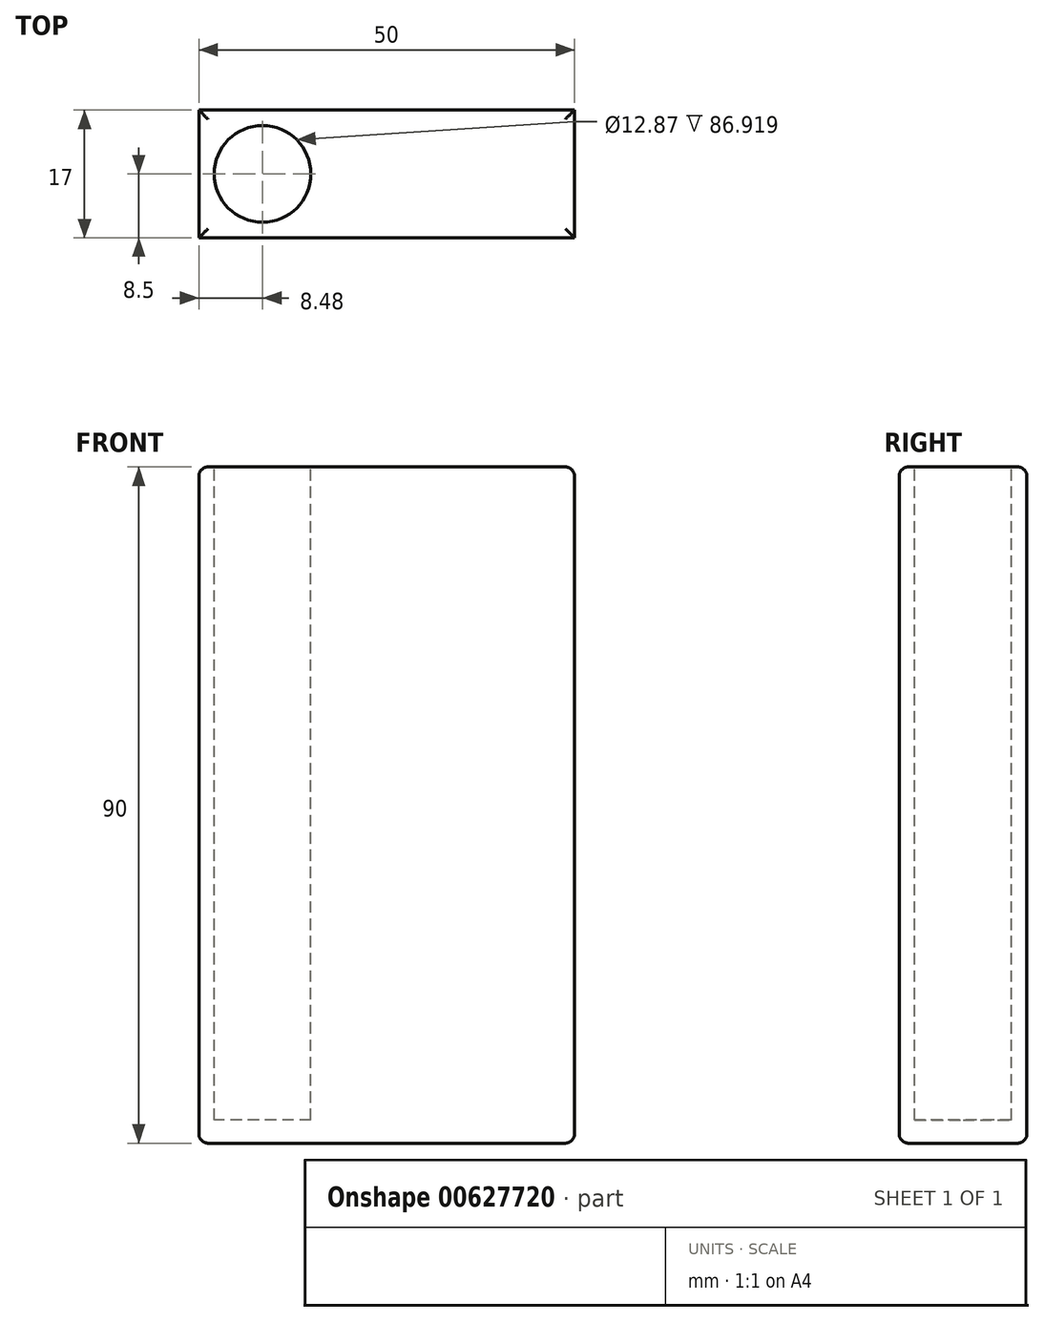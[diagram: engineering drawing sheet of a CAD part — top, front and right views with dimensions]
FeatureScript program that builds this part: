
annotation { "Feature Type Name" : "Feature", "Feature Type Description" : "" }
export const myFeature = defineFeature(function(context is Context, id is Id, definition is map)
    precondition{}
    {
        {
            var Q0;
            Q0=qCreatedBy(makeId("Front.planeOp"),FACE);
            var sketch = newSketch(context, id + "F0", { "sketchPlane" : qUnion([Q0])});
            skLineSegment(sketch, "E0.bottom", {"start": v(0, 90) * mm, "end": v(-50, 90) * mm});
            skLineSegment(sketch, "E0.top", {"start": v(0, 0) * mm, "end": v(-50, 0) * mm});
            skLineSegment(sketch, "E0.left", {"start": v(0, 90) * mm, "end": v(0, 0) * mm});
            skLineSegment(sketch, "E0.right", {"start": v(-50, 90) * mm, "end": v(-50, 0) * mm});
            skSolve(sketch);
        }
        {
            var Q0;
            Q0=makeQuery(id+"F0.imprint","IMPRINT",FACE,{"disambiguationData":[TD([[makeQuery(id+"F0.imprint","IMPRINT",EDGE,{"derivedFrom":sQuery(id+"F0.wireOp",EDGE,"E0.bottom")}),1.0]])]});
            extrude(context, id + "F1", {"entities" : qUnion([Q0]), "depth" : 17 * mm, "offsetDistance" : 25.4 * mm});
        }
        {
            var Q0;
            Q0=makeQuery(id+"F1.opExtrude","SWEPT_FACE",FACE,{"disambiguationData":[OSD([sQuery(id+"F0.wireOp",EDGE,"E0.bottom")])]});
            var Q1;
            Q1=makeQuery(id+"F1.opExtrude","SWEPT_FACE",FACE,{"disambiguationData":[OSD([sQuery(id+"F0.wireOp",EDGE,"E0.top")])]});
            fillet(context, id + "F2", {"entities" : qUnion([Q0, Q1]), "radius" : 1.23 * mm, "tangentPropagation" : true, "allowEdgeOverflow" : false});
        }
        {
            var Q0;
            Q0=makeQuery(id+"F1.opExtrude","SWEPT_FACE",FACE,{"disambiguationData":[OSD([sQuery(id+"F0.wireOp",EDGE,"E0.bottom")])]});
            var sketch = newSketch(context, id + "F3", { "sketchPlane" : qUnion([Q0])});
            skCircle(sketch, "E1", {"center": v(-41.52, -8.5) * mm, "radius": 6.43 * mm});
            skLineSegment(sketch, "E2", {"start": v(-48.77, -8.5) * mm, "end": v(-1.23, -8.5) * mm, "construction": true});
            skSolve(sketch);
        }
        {
            var Q0;
            Q0=makeQuery(id+"F3.imprint","IMPRINT",FACE,{"disambiguationData":[TD([[makeQuery(id+"F3.imprint","IMPRINT",EDGE,{"derivedFrom":sQuery(id+"F3.wireOp",EDGE,"E1")}),1.0]])]});
            extrude(context, id + "F4", {"entities" : qUnion([Q0]), "operationType" : NewBodyOperationType.REMOVE, "oppositeDirection" : true, "depth" : 86.92 * mm, "offsetDistance" : 25.4 * mm});
        }
    });
